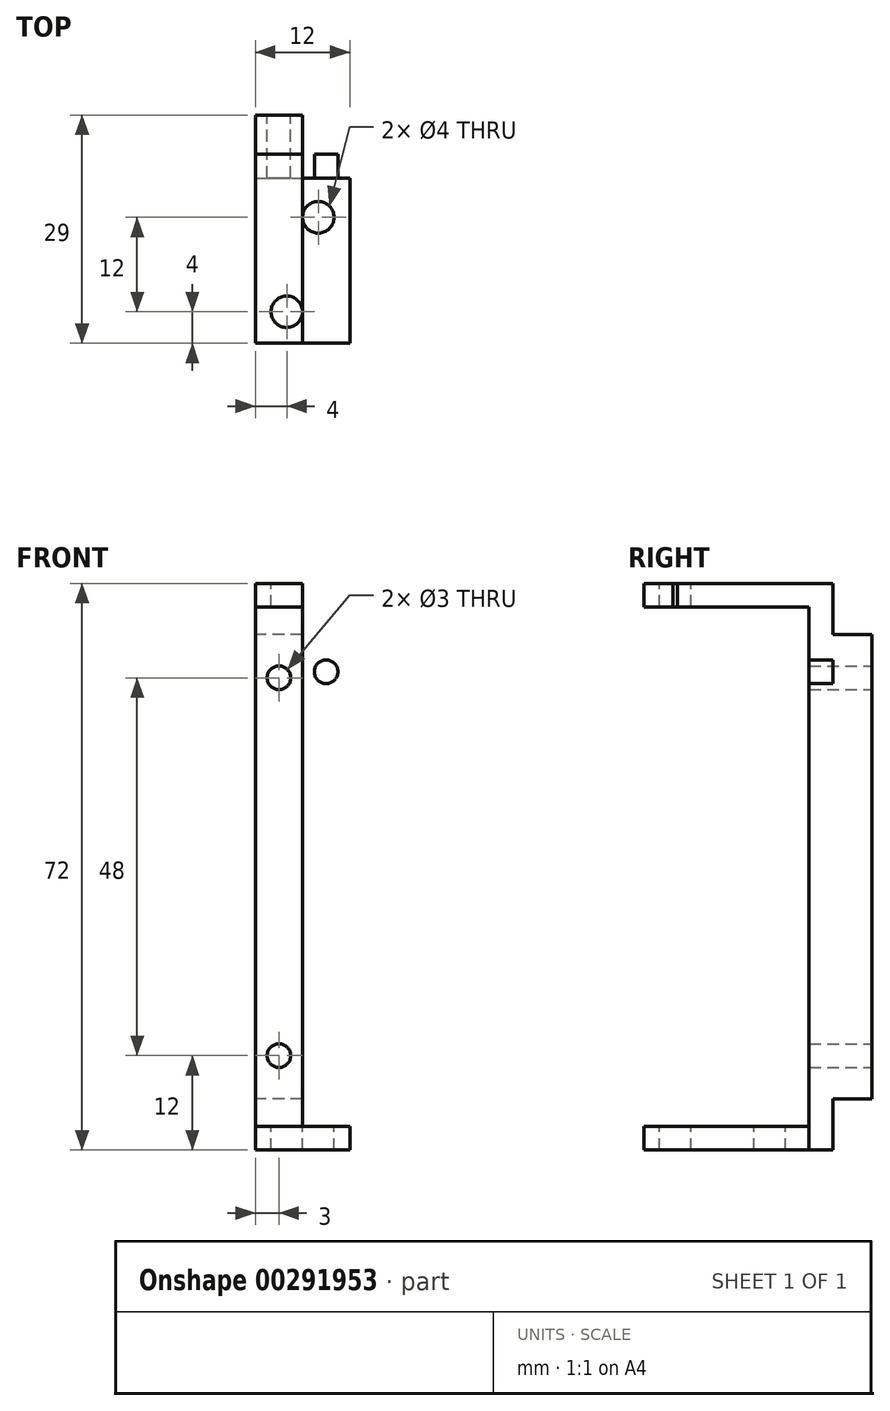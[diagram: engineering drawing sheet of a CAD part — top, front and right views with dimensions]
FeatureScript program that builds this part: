
annotation { "Feature Type Name" : "Feature", "Feature Type Description" : "" }
export const myFeature = defineFeature(function(context is Context, id is Id, definition is map)
    precondition{}
    {
        {
            var Q0;
            Q0=qCreatedBy(makeId("Right.planeOp"),FACE);
            var sketch = newSketch(context, id + "F0", { "sketchPlane" : qUnion([Q0])});
            skLineSegment(sketch, "E0", {"start": v(-10.5, 37.5) * mm, "end": v(18.5, 37.5) * mm});
            skLineSegment(sketch, "E1", {"start": v(18.5, 37.5) * mm, "end": v(18.5, -34.5) * mm});
            skLineSegment(sketch, "E2.0", {"start": v(10.5, 34.5) * mm, "end": v(10.5, -34.5) * mm});
            skLineSegment(sketch, "E2.1", {"start": v(-10.5, 34.5) * mm, "end": v(10.5, 34.5) * mm});
            skLineSegment(sketch, "E3", {"start": v(-10.5, 37.5) * mm, "end": v(-10.5, 34.5) * mm});
            skLineSegment(sketch, "E4", {"start": v(18.5, -34.5) * mm, "end": v(10.5, -34.5) * mm});
            skLineSegment(sketch, "E5", {"start": v(10.5, 0) * mm, "end": v(-14.36, 0) * mm, "construction": true});
            skLineSegment(sketch, "E6", {"start": v(0, 34.5) * mm, "end": v(0, -1.72) * mm, "construction": true});
            skSolve(sketch);
        }
        {
            var Q0;
            Q0=makeQuery(id+"F0.imprint","IMPRINT",FACE,{"disambiguationData":[TD([[makeQuery(id+"F0.imprint","IMPRINT",EDGE,{"derivedFrom":sQuery(id+"F0.wireOp",EDGE,"E0")}),-1.0]])]});
            extrude(context, id + "F1", {"entities" : qUnion([Q0]), "depth" : 12 * mm});
        }
        {
            var Q0;
            Q0=makeQuery(id+"F1.opExtrude","SWEPT_FACE",FACE,{"disambiguationData":[OSD([sQuery(id+"F0.wireOp",EDGE,"E0")])]});
            var sketch = newSketch(context, id + "F2", { "sketchPlane" : qUnion([Q0])});
            skLineSegment(sketch, "E7.bottom", {"start": v(0, 18.5) * mm, "end": v(6.02, 18.5) * mm});
            skLineSegment(sketch, "E7.top", {"start": v(0, 13.5) * mm, "end": v(6.02, 13.5) * mm});
            skLineSegment(sketch, "E7.left", {"start": v(0, 18.5) * mm, "end": v(0, 13.5) * mm});
            skLineSegment(sketch, "E7.right", {"start": v(6.02, 18.5) * mm, "end": v(6.02, 13.5) * mm});
            skSolve(sketch);
        }
        {
            var Q0;
            Q0=makeQuery(id+"F2.imprint","IMPRINT",FACE,{"disambiguationData":[TD([[makeQuery(id+"F2.imprint","IMPRINT",EDGE,{"derivedFrom":sQuery(id+"F2.wireOp",EDGE,"E7.bottom")}),1.0]])]});
            extrude(context, id + "F3", {"entities" : qUnion([Q0]), "operationType" : NewBodyOperationType.REMOVE, "oppositeDirection" : true, "depth" : 72 * mm});
        }
        {
            var Q0;
            Q0=makeQuery(id+"F1.opExtrude","SWEPT_FACE",FACE,{"disambiguationData":[OSD([sQuery(id+"F0.wireOp",EDGE,"E1")])]});
            var sketch = newSketch(context, id + "F4", { "sketchPlane" : qUnion([Q0])});
            skCircle(sketch, "E8", {"center": v(-9, 25.5) * mm, "radius": 1.5 * mm});
            skCircle(sketch, "E9", {"center": v(-9, -22.5) * mm, "radius": 1.5 * mm});
            skLineSegment(sketch, "E10", {"start": v(-9, 25.5) * mm, "end": v(-9, -22.5) * mm, "construction": true});
            skPoint(sketch, "E11", {"position": v(-9, 37.5) * mm});
            skLineSegment(sketch, "E12", {"start": v(-9, 25.5) * mm, "end": v(-9, 37.5) * mm, "construction": true});
            skSolve(sketch);
        }
        {
            var Q0;
            Q0=makeQuery(id+"F4.imprint","IMPRINT",FACE,{"disambiguationData":[TD([[makeQuery(id+"F4.imprint","IMPRINT",EDGE,{"derivedFrom":sQuery(id+"F4.wireOp",EDGE,"E8")}),1.0]])]});
            var Q1;
            Q1=makeQuery(id+"F4.imprint","IMPRINT",FACE,{"disambiguationData":[TD([[makeQuery(id+"F4.imprint","IMPRINT",EDGE,{"derivedFrom":sQuery(id+"F4.wireOp",EDGE,"E9")}),1.0]])]});
            extrude(context, id + "F5", {"entities" : qUnion([Q0, Q1]), "operationType" : NewBodyOperationType.REMOVE, "oppositeDirection" : true, "depth" : 25 * mm});
        }
        {
            var Q0;
            Q0=makeQuery(id+"F3.boolean.opBoolean","COPY",FACE,{"derivedFrom":makeQuery(id+"F3.opExtrude","SWEPT_FACE",FACE,{"disambiguationData":[OSD([sQuery(id+"F2.wireOp",EDGE,"E7.top")])]})});
            var sketch = newSketch(context, id + "F6", { "sketchPlane" : qUnion([Q0])});
            skCircle(sketch, "E13.0", {"center": v(-3, 26.27) * mm, "radius": 1.5 * mm});
            skCircle(sketch, "E14.0", {"center": v(-3, -23.27) * mm, "radius": 1.5 * mm});
            skLineSegment(sketch, "E15", {"start": v(-3, 37.5) * mm, "end": v(-3, 26.27) * mm, "construction": true});
            skLineSegment(sketch, "E16", {"start": v(-3, 26.27) * mm, "end": v(-3, -23.27) * mm, "construction": true});
            skSolve(sketch);
        }
        {
            var Q0;
            Q0=makeQuery(id+"F6.imprint","IMPRINT",FACE,{"disambiguationData":[TD([[makeQuery(id+"F6.imprint","IMPRINT",EDGE,{"derivedFrom":sQuery(id+"F6.wireOp",EDGE,"E14.0")}),1.0]])]});
            var Q1;
            Q1=makeQuery(id+"F6.imprint","IMPRINT",FACE,{"disambiguationData":[TD([[makeQuery(id+"F6.imprint","IMPRINT",EDGE,{"derivedFrom":sQuery(id+"F6.wireOp",EDGE,"E13.0")}),-1.0]])]});
            extrude(context, id + "F7", {"entities" : qUnion([Q0, Q1]), "operationType" : NewBodyOperationType.REMOVE, "oppositeDirection" : true, "depth" : 25 * mm});
        }
        {
            var Q0;
            Q0=makeQuery(id+"F1.opExtrude","SWEPT_FACE",FACE,{"disambiguationData":[OSD([sQuery(id+"F0.wireOp",EDGE,"E2.0")])]});
            var sketch = newSketch(context, id + "F8", { "sketchPlane" : qUnion([Q0])});
            skLineSegment(sketch, "E17.bottom", {"start": v(12, -34.5) * mm, "end": v(0, -34.5) * mm});
            skLineSegment(sketch, "E17.top", {"start": v(12, -31.5) * mm, "end": v(0, -31.5) * mm});
            skLineSegment(sketch, "E17.left", {"start": v(12, -34.5) * mm, "end": v(12, -31.5) * mm});
            skLineSegment(sketch, "E17.right", {"start": v(0, -34.5) * mm, "end": v(0, -31.5) * mm});
            skSolve(sketch);
        }
        {
            var Q0;
            Q0=makeQuery(id+"F8.imprint","IMPRINT",FACE,{"disambiguationData":[TD([[makeQuery(id+"F8.imprint","IMPRINT",EDGE,{"derivedFrom":sQuery(id+"F8.wireOp",EDGE,"E17.bottom")}),-1.0]])]});
            extrude(context, id + "F9", {"entities" : qUnion([Q0]), "operationType" : NewBodyOperationType.ADD, "depth" : 21 * mm});
        }
        {
            var Q0;
            Q0=makeQuery(id+"F1.opExtrude","SWEPT_FACE",FACE,{"disambiguationData":[OSD([sQuery(id+"F0.wireOp",EDGE,"E0")])]});
            var sketch = newSketch(context, id + "F10", { "sketchPlane" : qUnion([Q0])});
            skCircle(sketch, "E18", {"center": v(4, 5.5) * mm, "radius": 2 * mm});
            skCircle(sketch, "E19", {"center": v(8, -6.5) * mm, "radius": 2 * mm});
            skSolve(sketch);
        }
        {
            var Q0;
            Q0=makeQuery(id+"F10.imprint","IMPRINT",FACE,{"disambiguationData":[TD([[makeQuery(id+"F10.imprint","IMPRINT",EDGE,{"derivedFrom":sQuery(id+"F10.wireOp",EDGE,"E18")}),1.0]])]});
            var Q1;
            Q1=makeQuery(id+"F10.imprint","IMPRINT",FACE,{"disambiguationData":[TD([[makeQuery(id+"F10.imprint","IMPRINT",EDGE,{"derivedFrom":sQuery(id+"F10.wireOp",EDGE,"E19")}),1.0]])]});
            extrude(context, id + "F11", {"entities" : qUnion([Q0, Q1]), "operationType" : NewBodyOperationType.REMOVE, "oppositeDirection" : true, "depth" : 72 * mm});
        }
        {
            var Q0;
            Q0=makeQuery(id+"F1.opExtrude","SWEPT_BODY",BODY,{"disambiguationData":[OSD([sQuery(id+"F0.wireOp",EDGE,"E0"),sQuery(id+"F0.wireOp",EDGE,"E1"),sQuery(id+"F0.wireOp",EDGE,"E2.0"),sQuery(id+"F0.wireOp",EDGE,"E2.1"),sQuery(id+"F0.wireOp",EDGE,"E3"),sQuery(id+"F0.wireOp",EDGE,"E4")])]});
            var Q1;
            Q1=makeQuery(id+"F1.opExtrude","CAP_FACE",FACE,{"disambiguationData":[OSD([sQuery(id+"F0.wireOp",EDGE,"E0"),sQuery(id+"F0.wireOp",EDGE,"E1"),sQuery(id+"F0.wireOp",EDGE,"E2.0"),sQuery(id+"F0.wireOp",EDGE,"E2.1"),sQuery(id+"F0.wireOp",EDGE,"E3"),sQuery(id+"F0.wireOp",EDGE,"E4")])],"isStart":false});
            mirror(context, id + "F12", {"entities" : qUnion([Q0]), "mirrorPlane" : qUnion([Q1])});
        }
        {
            var Q0;
            Q0=makeQuery(id+"F1.opExtrude","SWEPT_BODY",BODY,{"disambiguationData":[OSD([sQuery(id+"F0.wireOp",EDGE,"E0"),sQuery(id+"F0.wireOp",EDGE,"E1"),sQuery(id+"F0.wireOp",EDGE,"E2.0"),sQuery(id+"F0.wireOp",EDGE,"E2.1"),sQuery(id+"F0.wireOp",EDGE,"E3"),sQuery(id+"F0.wireOp",EDGE,"E4")])]});
            deleteBodies(context, id + "F13", {"entities" : qUnion([Q0])});
        }
        {
            var Q0;
            Q0=makeQuery(id+"F12.opPattern","COPY",FACE,{"derivedFrom":makeQuery(id+"F1.opExtrude","SWEPT_FACE",FACE,{"disambiguationData":[OSD([sQuery(id+"F0.wireOp",EDGE,"E1")])]}),"instanceName":"1"});
            var sketch = newSketch(context, id + "F14", { "sketchPlane" : qUnion([Q0])});
            skLineSegment(sketch, "E20.bottom", {"start": v(-17.98, 37.5) * mm, "end": v(-12, 37.5) * mm});
            skLineSegment(sketch, "E20.top", {"start": v(-17.98, 31) * mm, "end": v(-12, 31) * mm});
            skLineSegment(sketch, "E20.left", {"start": v(-17.98, 37.5) * mm, "end": v(-17.98, 31) * mm});
            skLineSegment(sketch, "E20.right", {"start": v(-12, 37.5) * mm, "end": v(-12, 31) * mm});
            skLineSegment(sketch, "E21.bottom", {"start": v(-17.98, -34.5) * mm, "end": v(-12, -34.5) * mm});
            skLineSegment(sketch, "E21.top", {"start": v(-17.98, -28) * mm, "end": v(-12, -28) * mm});
            skLineSegment(sketch, "E21.left", {"start": v(-17.98, -34.5) * mm, "end": v(-17.98, -28) * mm});
            skLineSegment(sketch, "E21.right", {"start": v(-12, -34.5) * mm, "end": v(-12, -28) * mm});
            skSolve(sketch);
        }
        {
            var Q0;
            Q0=qSketchRegion(id+"F14",true);
            extrude(context, id + "F15", {"entities" : qUnion([Q0]), "operationType" : NewBodyOperationType.REMOVE, "oppositeDirection" : true, "depth" : 5 * mm});
        }
    });
